# Revit family: HVAC_Heat-Pump_Enertech_CTC-EcoAir-410-420
name_source: partatom
category: Specialty Equipment
revit_build: Autodesk Revit 2018 (Build: 20190510_1515(x64)
units: mm (PartAtom-declared; Revit-internal decimal feet)

## family parameters
Always vertical = Yes
Cut with Voids When Loaded = No
OmniClass Number = 23.75.00.00
OmniClass Title = Climate Control (HVAC)
Part Type = Normal
Room Calculation Point = No
Round Connector Dimension = Use Diameter
Shared = No
Work Plane-Based = No

## types (4) — shared parameters
AssetType = Fixed
BIMObjectName = HVAC_Water-Heaters_Enertech_CTC-EcoAir-410-420
Brand = CTC
BrineSystem_Min_MaxPressure = 0.2 - 3.0 bar
Capacity = Fixed
Category = Heat Pumps, Air-to-water
Color = grey
Description = CTC EcoAir 400, a series of on/off air-to-water heat pumps available in six sizes with outputs of 6-17 kW. Model: 406-420
DurationUnit = Year
HasProtectiveEarth = Yes
IP_Code = IP X4
IfcExportAs = IfcElectricalDeviceCommon
IfcExportType = HEATER
Manufacturer = Enertech AB
ManufacturerCountry = Sweden
ManufacturerName = Enertech AB
ManufacturerURL = https://ctc.se
Material = Steel/copper
MaxOperatingPressureThermalStore = 3 bar
NBSDescription = Air to water heat pumps
NBSReference = 90-40-40/320
Name = CTC-EcoAir-410-420
NominalCurrent = 0 A
NominalDepth = 645 mm  [stored 2.11614 ft]
NominalFrequencyRange = 50 Hz
NominalHeight = 1180 mm  [stored 3.87139 ft]
NominalWidth = 1375 mm  [stored 4.51115 ft]
PhaseAngle = 0.00°
PowerFactor = 0 W
ProductInformation = CTC EcoAir 400, a series of on/off air-to-water heat pumps available in six sizes with outputs of 6-17 kW. Model: 406-420
PumpMainMaterial = Stainless Steel
RefrigerantType = R407C
Revision = 5
Shape = Rectangular
Touchscreen = no
UNSPSCCode = 40101806
URL = https://ctc-heating.com
Uniclass2 = Pr_40_70_65
Uniclass2015Description = Preparation catering equipment
Uniclass2015Reference = Pr_40_70_65
UsageCurrent = 0 A
Version = 1
VersionDate = 26/08/2021
WarrantyDurationUnit = Year
zero-valued in all types: Cost

## per-type parameters (varying)
- CTC EcoAir 415 - 400V3N: AirFlow=5400 m3/h; CO2Equivalent=6.032 tonnes; COP=4.76; EANNumber=7333077090142; EnergyClassHeatingWithControl=A++ / A+; EnergyClassHeatingWithoutControl=A+ / A+; InPutPower=3.5 kW; MaxStartingCurrent=24.0 A; Model=CTC EcoAir 415; ModelNumber=585600004; NominalVoltage=400 V; NumberOfPoles=3; RatedCurrent=10 A; RatedHeatOutputModerate=13 kW; RatedVoltage=1200 V; RefrigerantQuantity=3.4 kg; SCOPCold=3.3; SCOPModerate=3.8; SCOPWarm=4.6; Size=645x1375x1180 mm; Sound pressureLPA 10m=39 dB; Sound pressureLPA 5m=45 dB; SoundPowerLWA=64 dB; SpecifiedOutput=15.9 kW; WaterVolumeHeathingSystem=3.9 liter; Weight=187 kg
- CTC EcoAir 420 - 400V3N: AirFlow=6200 m3/h; CO2Equivalent=6.209 tonnes; COP=4.62; EANNumber=7333077090159; EnergyClassHeatingWithControl=A+ / A+; EnergyClassHeatingWithoutControl=A+ / A+; InPutPower=4.1 kW; MaxStartingCurrent=24.4 A; Model=CTC EcoAir 420; ModelNumber=585600005; NominalVoltage=400 V; NumberOfPoles=3; RatedCurrent=12 A; RatedHeatOutputModerate=14 kW; RatedVoltage=1200 V; RefrigerantQuantity=3.5 kg; SCOPCold=3.3; SCOPModerate=3.7; SCOPWarm=4.5; Size=645x1375x1180 mm; Sound pressureLPA 10m=41 dB; Sound pressureLPA 5m=47 dB; SoundPowerLWA=66 dB; SpecifiedOutput=17.6 kW; WaterVolumeHeathingSystem=4.5 liter; Weight=190 kg
- CTC EcoAir 410 - 400V3N: AirFlow=4100 m3/h; CO2Equivalent=4.790 tonnes; COP=4.86; EANNumber=7333077090135; EnergyClassHeatingWithControl=A++ / A++; EnergyClassHeatingWithoutControl=A++ / A++; InPutPower=2.4 kW; MaxStartingCurrent=14.3 A; Model=CTC EcoAir 410; ModelNumber=585600003; NominalVoltage=400 V; NumberOfPoles=3; RatedCurrent=8 A; RatedHeatOutputModerate=10 kW; RatedVoltage=1200 V; RefrigerantQuantity=2.7 kg; SCOPCold=3.5; SCOPModerate=3.9; SCOPWarm=4.8; Size=545x1245x1080 mm; Sound pressureLPA 10m=33 dB; Sound pressureLPA 5m=39 dB; SoundPowerLWA=58 dB; SpecifiedOutput=11.5 kW; WaterVolumeHeathingSystem=2.8 liter; Weight=180 kg
- CTC EcoAir 410 - 230V1N: AirFlow=4100 m3/h; CO2Equivalent=4.790 tonnes; COP=4.86; EANNumber=7333077000127; EnergyClassHeatingWithControl=A++ / A+; EnergyClassHeatingWithoutControl=A++ / A+; InPutPower=2.4 kW; MaxStartingCurrent=23.5 A; Model=CTC EcoAir 410; ModelNumber=585600013; NominalVoltage=230 V; NumberOfPoles=1; RatedCurrent=19 A; RatedVoltage=230 V; RefrigerantQuantity=2.7 kg; SCOPCold=3.5; SCOPModerate=3.9; SCOPWarm=4.8; Size=545x1245x1080 mm; Sound pressureLPA 10m=33 dB; Sound pressureLPA 5m=39 dB; SoundPowerLWA=58 dB; SpecifiedOutput=11.5 kW; WaterVolumeHeathingSystem=2.8 liter; Weight=180 kg

note: [stored X ft] marks values corroborated as IEEE doubles in the binary element streams (Revit-internal decimal feet)

## geometry (parser evidence)
native form markers: Sweep x3
no freeform markers — native parametric forms only
